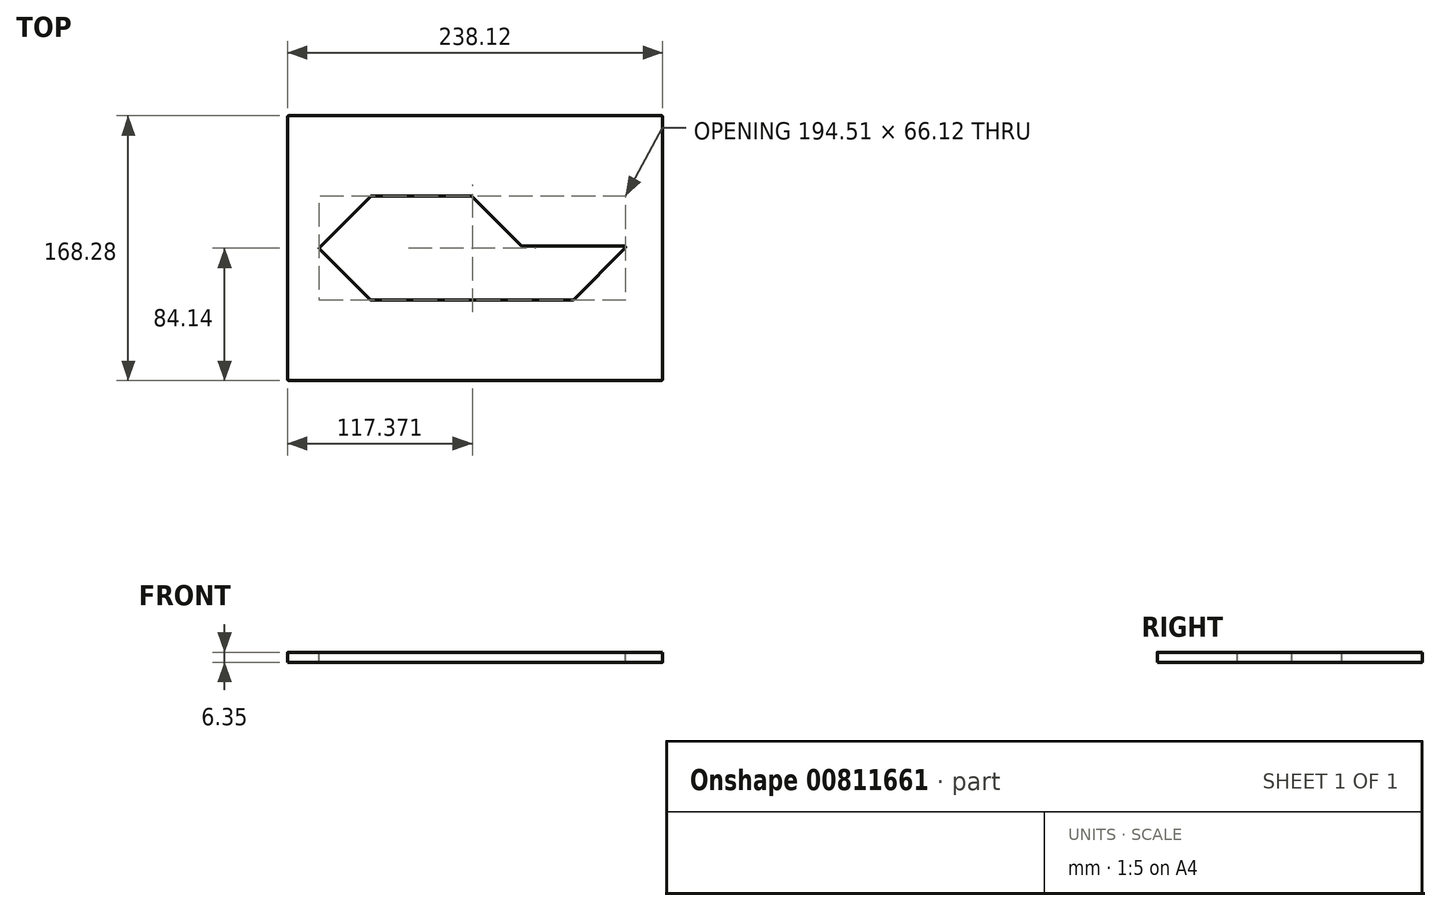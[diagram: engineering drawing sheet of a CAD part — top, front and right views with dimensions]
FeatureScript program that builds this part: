
annotation { "Feature Type Name" : "Feature", "Feature Type Description" : "" }
export const myFeature = defineFeature(function(context is Context, id is Id, definition is map)
    precondition{}
    {
        {
            var Q0;
            Q0=qCreatedBy(makeId("Top.planeOp"),FACE);
            var sketch = newSketch(context, id + "F0", { "sketchPlane" : qUnion([Q0])});
            skLineSegment(sketch, "E0.bottom", {"start": v(-118.28, 84.14) * mm, "end": v(118.28, 84.14) * mm});
            skLineSegment(sketch, "E0.top", {"start": v(-118.28, -84.14) * mm, "end": v(118.28, -84.14) * mm});
            skLineSegment(sketch, "E0.left", {"start": v(-119.06, 83.35) * mm, "end": v(-119.06, -83.35) * mm});
            skLineSegment(sketch, "E0.right", {"start": v(119.06, 83.35) * mm, "end": v(119.06, -83.35) * mm});
            skPoint(sketch, "E0.middle", {"position": v(0, 0) * mm});
            skPoint(sketch, "E1.visualSharp", {"position": v(-119.06, 84.14) * mm});
            skArc(sketch, "E1.filletArc", {"start": v(-118.28, 84.14) * mm, "mid": v(-118.83, 83.9) * mm, "end": v(-119.06, 83.35) * mm});
            skPoint(sketch, "E2.visualSharp", {"position": v(119.06, 84.14) * mm});
            skArc(sketch, "E2.filletArc", {"start": v(119.06, 83.35) * mm, "mid": v(118.83, 83.9) * mm, "end": v(118.28, 84.14) * mm});
            skPoint(sketch, "E3.visualSharp", {"position": v(119.06, -84.14) * mm});
            skArc(sketch, "E3.filletArc", {"start": v(118.28, -84.14) * mm, "mid": v(118.83, -83.9) * mm, "end": v(119.06, -83.35) * mm});
            skPoint(sketch, "E4.visualSharp", {"position": v(-119.06, -84.14) * mm});
            skArc(sketch, "E4.filletArc", {"start": v(-119.06, -83.35) * mm, "mid": v(-118.83, -83.9) * mm, "end": v(-118.28, -84.14) * mm});
            skSolve(sketch);
        }
        {
            var Q0;
            Q0 = qSketchRegion(id + "F0", true);
            extrude(context, id + "F1", {"entities" : qUnion([Q0]), "depth" : 6.35 * mm, "offsetDistance" : 25.4 * mm});
        }
        {
            var Q0;
            Q0=makeQuery(id+"F1.opExtrude","CAP_FACE",FACE,{"disambiguationData":[OSD([sQuery(id+"F0.wireOp",EDGE,"E0.bottom"),sQuery(id+"F0.wireOp",EDGE,"E0.top"),sQuery(id+"F0.wireOp",EDGE,"E0.left"),sQuery(id+"F0.wireOp",EDGE,"E0.right"),sQuery(id+"F0.wireOp",EDGE,"E1.filletArc"),sQuery(id+"F0.wireOp",EDGE,"E2.filletArc"),sQuery(id+"F0.wireOp",EDGE,"E3.filletArc"),sQuery(id+"F0.wireOp",EDGE,"E4.filletArc")])],"isStart":false});
            var sketch = newSketch(context, id + "F2", { "sketchPlane" : qUnion([Q0])});
            skLineSegment(sketch, "E5", {"start": v(-65.68, 31.8) * mm, "end": v(-97.47, 0) * mm});
            skLineSegment(sketch, "E6", {"start": v(-97.47, 0) * mm, "end": v(-65.68, -31.8) * mm});
            skLineSegment(sketch, "E7", {"start": v(-65.68, -31.8) * mm, "end": v(61.83, -31.8) * mm});
            skLineSegment(sketch, "E8", {"start": v(61.83, -31.8) * mm, "end": v(93.62, 0) * mm});
            skLineSegment(sketch, "E9", {"start": v(93.62, 0) * mm, "end": v(29.1, 0) * mm});
            skLineSegment(sketch, "E10", {"start": v(29.1, 0) * mm, "end": v(-2.7, 31.8) * mm});
            skLineSegment(sketch, "E11", {"start": v(-2.7, 31.8) * mm, "end": v(-65.68, 31.8) * mm});
            skSolve(sketch);
        }
        {
            var Q0;
            Q0 = qSketchRegion(id + "F2", true);
            extrude(context, id + "F3", {"entities" : qUnion([Q0]), "operationType" : NewBodyOperationType.REMOVE, "oppositeDirection" : true, "depth" : 25.4 * mm, "offsetDistance" : 25.4 * mm});
        }
        {
            var Q0;
            Q0=makeQuery(id+"F1.opExtrude","CAP_FACE",FACE,{"disambiguationData":[OSD([sQuery(id+"F0.wireOp",EDGE,"E0.bottom"),sQuery(id+"F0.wireOp",EDGE,"E0.top"),sQuery(id+"F0.wireOp",EDGE,"E0.left"),sQuery(id+"F0.wireOp",EDGE,"E0.right"),sQuery(id+"F0.wireOp",EDGE,"E1.filletArc"),sQuery(id+"F0.wireOp",EDGE,"E2.filletArc"),sQuery(id+"F0.wireOp",EDGE,"E3.filletArc"),sQuery(id+"F0.wireOp",EDGE,"E4.filletArc")])],"isStart":false});
            var sketch = newSketch(context, id + "F4", { "sketchPlane" : qUnion([Q0])});
            skLineSegment(sketch, "E12.0", {"start": v(29.4, 1.5) * mm, "end": v(-1.93, 32.83) * mm});
            skLineSegment(sketch, "E12.1", {"start": v(94.78, 1.27) * mm, "end": v(29.95, 1.27) * mm});
            skLineSegment(sketch, "E12.2", {"start": v(-66.44, 32.83) * mm, "end": v(-98.71, 0.56) * mm});
            skLineSegment(sketch, "E12.3", {"start": v(-98.71, -0.56) * mm, "end": v(-66.44, -32.83) * mm});
            skLineSegment(sketch, "E12.4", {"start": v(-65.88, -33.06) * mm, "end": v(62.03, -33.06) * mm});
            skLineSegment(sketch, "E12.5", {"start": v(-2.5, 33.06) * mm, "end": v(-65.88, 33.06) * mm});
            skLineSegment(sketch, "E12.6", {"start": v(62.58, -32.83) * mm, "end": v(95.34, -0.07) * mm});
            skPoint(sketch, "E13.visualSharp", {"position": v(96.68, 1.27) * mm});
            skArc(sketch, "E13.filletArc", {"start": v(95.34, -0.07) * mm, "mid": v(95.5, 0.78) * mm, "end": v(94.78, 1.27) * mm});
            skPoint(sketch, "E14.visualSharp", {"position": v(62.35, -33.06) * mm});
            skArc(sketch, "E14.filletArc", {"start": v(62.03, -33.06) * mm, "mid": v(62.33, -33) * mm, "end": v(62.58, -32.83) * mm});
            skPoint(sketch, "E15.visualSharp", {"position": v(-66.2, -33.06) * mm});
            skArc(sketch, "E15.filletArc", {"start": v(-66.44, -32.83) * mm, "mid": v(-66.18, -33) * mm, "end": v(-65.88, -33.06) * mm});
            skPoint(sketch, "E16.visualSharp", {"position": v(-99.27, 0) * mm});
            skArc(sketch, "E16.filletArc", {"start": v(-98.71, 0.56) * mm, "mid": v(-98.94, 0) * mm, "end": v(-98.71, -0.56) * mm});
            skPoint(sketch, "E17.visualSharp", {"position": v(-66.2, 33.06) * mm});
            skArc(sketch, "E17.filletArc", {"start": v(-65.88, 33.06) * mm, "mid": v(-66.18, 33) * mm, "end": v(-66.44, 32.83) * mm});
            skPoint(sketch, "E18.visualSharp", {"position": v(-2.16, 33.06) * mm});
            skArc(sketch, "E18.filletArc", {"start": v(-1.93, 32.83) * mm, "mid": v(-2.19, 33) * mm, "end": v(-2.5, 33.06) * mm});
            skPoint(sketch, "E19.visualSharp", {"position": v(29.63, 1.27) * mm});
            skArc(sketch, "E19.filletArc", {"start": v(29.4, 1.5) * mm, "mid": v(29.65, 1.33) * mm, "end": v(29.95, 1.27) * mm});
            skSolve(sketch);
        }
        {
            var Q0;
            Q0 = qSketchRegion(id + "F4", true);
            extrude(context, id + "F5", {"entities" : qUnion([Q0]), "operationType" : NewBodyOperationType.REMOVE, "oppositeDirection" : true, "depth" : 25.4 * mm, "offsetDistance" : 25.4 * mm});
        }
    });
